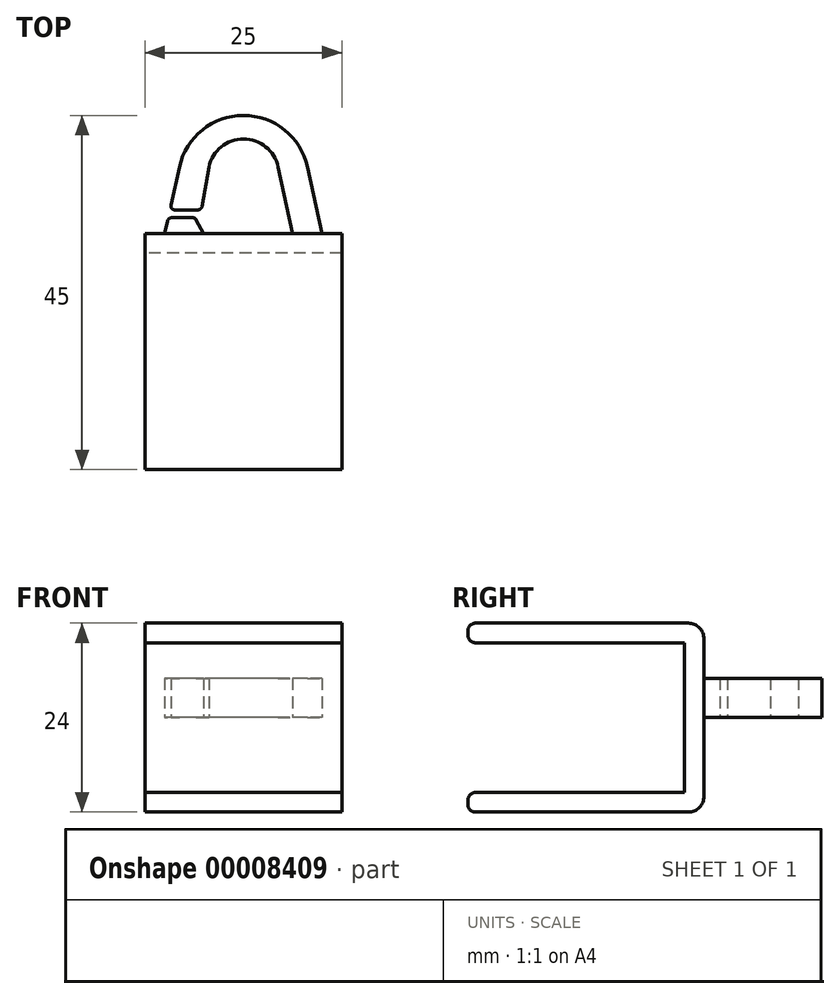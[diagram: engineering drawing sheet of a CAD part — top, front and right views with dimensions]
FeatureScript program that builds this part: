
annotation { "Feature Type Name" : "Feature", "Feature Type Description" : "" }
export const myFeature = defineFeature(function(context is Context, id is Id, definition is map)
    precondition{}
    {
        {
            var Q0;
            Q0=qCreatedBy(makeId("Right.planeOp"),FACE);
            var sketch = newSketch(context, id + "F0", { "sketchPlane" : qUnion([Q0])});
            skLineSegment(sketch, "E0.bottom", {"start": v(27.5, 9.5) * mm, "end": v(30, 9.5) * mm, "construction": true});
            skLineSegment(sketch, "E0.top", {"start": v(27.5, -9.5) * mm, "end": v(30, -9.5) * mm, "construction": true});
            skLineSegment(sketch, "E0.left", {"start": v(27.5, 9.5) * mm, "end": v(27.5, -9.5) * mm});
            skLineSegment(sketch, "E0.right", {"start": v(30, 9.5) * mm, "end": v(30, -2) * mm});
            skLineSegment(sketch, "E1.bottom", {"start": v(27.5, 9.5) * mm, "end": v(1, 9.5) * mm});
            skLineSegment(sketch, "E1.top", {"start": v(28, 12) * mm, "end": v(1, 12) * mm});
            skLineSegment(sketch, "E1.left", {"start": v(30, 9.5) * mm, "end": v(30, 10) * mm});
            skLineSegment(sketch, "E1.right", {"start": v(0, 10.5) * mm, "end": v(0, 11) * mm});
            skLineSegment(sketch, "E2.bottom", {"start": v(27.5, -9.5) * mm, "end": v(1, -9.5) * mm});
            skLineSegment(sketch, "E2.top", {"start": v(28, -12) * mm, "end": v(1, -12) * mm});
            skLineSegment(sketch, "E2.left", {"start": v(30, -9.5) * mm, "end": v(30, -10) * mm});
            skLineSegment(sketch, "E2.right", {"start": v(0, -10.5) * mm, "end": v(0, -11) * mm});
            skLineSegment(sketch, "E3", {"start": v(0, 9.5) * mm, "end": v(0, -9.5) * mm, "construction": true});
            skPoint(sketch, "E4", {"position": v(0, 0) * mm});
            skPoint(sketch, "E5.visualSharp", {"position": v(0, 9.5) * mm});
            skArc(sketch, "E5.filletArc", {"start": v(0, 10.5) * mm, "mid": v(0.3, 9.8) * mm, "end": v(1, 9.5) * mm});
            skPoint(sketch, "E6.visualSharp", {"position": v(0, -9.5) * mm});
            skArc(sketch, "E6.filletArc", {"start": v(1, -9.5) * mm, "mid": v(0.3, -9.8) * mm, "end": v(0, -10.5) * mm});
            skPoint(sketch, "E7.visualSharp", {"position": v(0, -12) * mm});
            skArc(sketch, "E7.filletArc", {"start": v(0, -11) * mm, "mid": v(0.3, -11.7) * mm, "end": v(1, -12) * mm});
            skPoint(sketch, "E8.visualSharp", {"position": v(0, 12) * mm});
            skArc(sketch, "E8.filletArc", {"start": v(1, 12) * mm, "mid": v(0.3, 11.7) * mm, "end": v(0, 11) * mm});
            skPoint(sketch, "E9.visualSharp", {"position": v(30, 12) * mm});
            skArc(sketch, "E9.filletArc", {"start": v(30, 10) * mm, "mid": v(29.41, 11.41) * mm, "end": v(28, 12) * mm});
            skPoint(sketch, "E10.visualSharp", {"position": v(30, -12) * mm});
            skArc(sketch, "E10.filletArc", {"start": v(28, -12) * mm, "mid": v(29.41, -11.41) * mm, "end": v(30, -10) * mm});
            skLineSegment(sketch, "E11", {"start": v(14.5, 12) * mm, "end": v(14.5, 9.5) * mm, "construction": true});
            skLineSegment(sketch, "E12", {"start": v(14.5, -12) * mm, "end": v(14.5, -9.5) * mm, "construction": true});
            skLineSegment(sketch, "E13.trimOffspring", {"start": v(30, -2) * mm, "end": v(30, -9.5) * mm});
            skSolve(sketch);
        }
        {
            var Q0;
            Q0=makeQuery(id+"F0.imprint","IMPRINT",FACE,{"disambiguationData":[TD([[makeQuery(id+"F0.imprint","IMPRINT",EDGE,{"derivedFrom":sQuery(id+"F0.wireOp",EDGE,"E0.left")}),1.0]])]});
            extrude(context, id + "F1", {"entities" : qUnion([Q0]), "depth" : 25 * mm});
        }
        {
            var Q0;
            Q0=qCreatedBy(makeId("Top.planeOp"),FACE);
            var sketch = newSketch(context, id + "F2", { "sketchPlane" : qUnion([Q0])});
            skArc(sketch, "E14", {"start": v(20.64, 38.46) * mm, "mid": v(12.5, 45) * mm, "end": v(4.36, 38.46) * mm});
            skLineSegment(sketch, "E15", {"start": v(20.64, 38.46) * mm, "end": v(4.36, 38.46) * mm, "construction": true});
            skLineSegment(sketch, "E16", {"start": v(20.64, 38.46) * mm, "end": v(22.5, 30) * mm});
            skLineSegment(sketch, "E17", {"start": v(22.5, 30) * mm, "end": v(18.75, 30) * mm});
            skLineSegment(sketch, "E18", {"start": v(2.5, 30) * mm, "end": v(2.85, 31.6) * mm});
            skLineSegment(sketch, "E19", {"start": v(12.5, 30) * mm, "end": v(12.5, 45) * mm, "construction": true});
            skArc(sketch, "E20", {"start": v(16.9, 38.46) * mm, "mid": v(12.5, 42) * mm, "end": v(8.1, 38.46) * mm});
            skLineSegment(sketch, "E21", {"start": v(16.9, 38.46) * mm, "end": v(18.75, 30) * mm});
            skLineSegment(sketch, "E22.trimOffspring", {"start": v(7.45, 30) * mm, "end": v(2.5, 30) * mm});
            skLineSegment(sketch, "E23", {"start": v(6.07, 32) * mm, "end": v(3.34, 32) * mm});
            skLineSegment(sketch, "E24", {"start": v(6.72, 33) * mm, "end": v(3.78, 33) * mm});
            skLineSegment(sketch, "E25.trimOffspring", {"start": v(3.3, 33.6) * mm, "end": v(4.36, 38.46) * mm});
            skLineSegment(sketch, "E26.trimOffspring", {"start": v(7.21, 33.41) * mm, "end": v(8.1, 38.46) * mm});
            skLineSegment(sketch, "E27", {"start": v(6.69, 32) * mm, "end": v(7.14, 33) * mm, "construction": true});
            skLineSegment(sketch, "E28", {"start": v(3.16, 33) * mm, "end": v(2.94, 32) * mm, "construction": true});
            skPoint(sketch, "E29.visualSharp", {"position": v(6.69, 32) * mm});
            skArc(sketch, "E29.filletArc", {"start": v(6.5, 31.74) * mm, "mid": v(6.32, 31.93) * mm, "end": v(6.07, 32) * mm});
            skPoint(sketch, "E30.visualSharp", {"position": v(2.94, 32) * mm});
            skArc(sketch, "E30.filletArc", {"start": v(3.34, 32) * mm, "mid": v(3.03, 31.89) * mm, "end": v(2.85, 31.6) * mm});
            skPoint(sketch, "E31.visualSharp", {"position": v(3.16, 33) * mm});
            skArc(sketch, "E31.filletArc", {"start": v(3.3, 33.6) * mm, "mid": v(3.4, 33.19) * mm, "end": v(3.78, 33) * mm});
            skPoint(sketch, "E32.visualSharp", {"position": v(7.14, 33) * mm});
            skArc(sketch, "E32.filletArc", {"start": v(6.72, 33) * mm, "mid": v(7.04, 33.12) * mm, "end": v(7.21, 33.41) * mm});
            skLineSegment(sketch, "E33", {"start": v(6.5, 31.74) * mm, "end": v(7.45, 30) * mm});
            skSolve(sketch);
        }
        {
            var Q0;
            Q0 = qSketchRegion(id + "F2", true);
            extrude(context, id + "F3", {"entities" : qUnion([Q0]), "operationType" : NewBodyOperationType.ADD, "depth" : 5 * mm});
        }
    });
